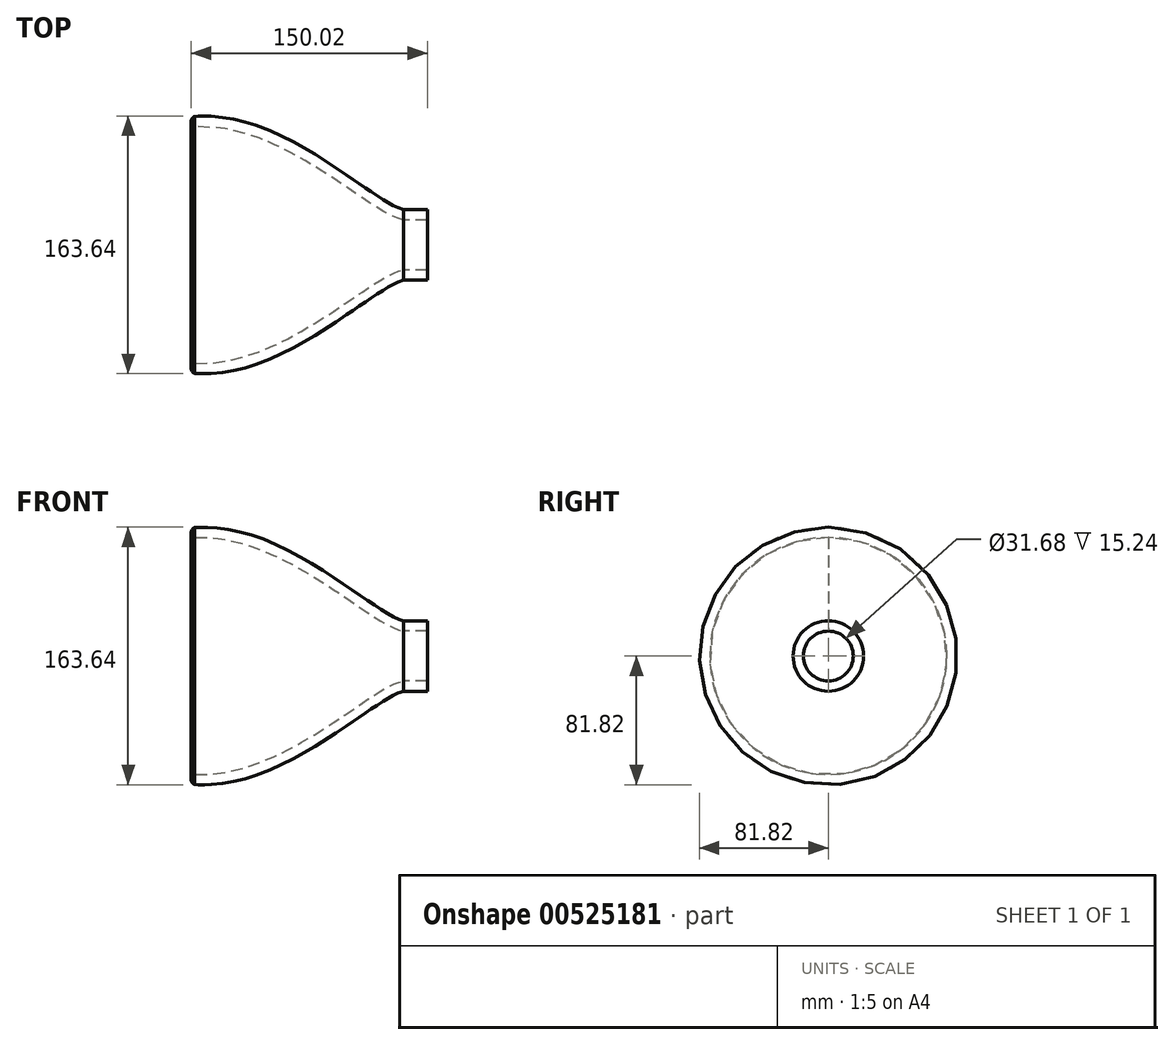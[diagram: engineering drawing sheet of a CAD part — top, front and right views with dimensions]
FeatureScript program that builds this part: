
annotation { "Feature Type Name" : "Feature", "Feature Type Description" : "" }
export const myFeature = defineFeature(function(context is Context, id is Id, definition is map)
    precondition{}
    {
        {
            var Q0;
            Q0=qCreatedBy(makeId("Top.planeOp"),FACE);
            var sketch = newSketch(context, id + "F0", { "sketchPlane" : qUnion([Q0])});
            skLineSegment(sketch, "E0", {"start": v(-136.45, 0) * mm, "end": v(145.54, 0) * mm, "construction": true});
            skLineSegment(sketch, "E1", {"start": v(76.07, 22.38) * mm, "end": v(76.07, 16.02) * mm});
            skLineSegment(sketch, "E2.bottom", {"start": v(76.07, 22.38) * mm, "end": v(91.31, 22.38) * mm});
            skLineSegment(sketch, "E2.top", {"start": v(76.07, 15.84) * mm, "end": v(91.31, 15.84) * mm});
            skLineSegment(sketch, "E2.left", {"start": v(76.07, 22.38) * mm, "end": v(76.07, 15.84) * mm});
            skLineSegment(sketch, "E2.right", {"start": v(91.31, 22.38) * mm, "end": v(91.31, 15.84) * mm});
            skArc(sketch, "E3", {"start": v(-56.47, 81.64) * mm, "mid": v(-58.7, 78.37) * mm, "end": v(-56.2, 75.3) * mm});
            skFitSpline(sketch, "E4", {"points": [v(-56.2, 75.3) * mm, v(76.07, 15.84) * mm], "startDerivative": vector(168.63, 7) * mm, "endDerivative": vector(67.94, -13.53) * mm});
            skFitSpline(sketch, "E5.0", {"points": [v(-56.47, 81.64) * mm, v(-52.68, 81.8) * mm, v(-45.14, 81.6) * mm, v(-30.35, 79.48) * mm, v(-12.51, 74.04) * mm, v(7.6, 64.57) * mm, v(26.2, 53.54) * mm, v(40.2, 44.18) * mm, v(50.34, 37.28) * mm, v(57.35, 32.56) * mm, v(63.71, 28.48) * mm, v(69.33, 25.22) * mm, v(73.26, 23.34) * mm, v(75.82, 22.42) * mm, v(76.86, 22.16) * mm, v(77.31, 22.07) * mm]});
            skSolve(sketch);
        }
        {
            var Q0;
            Q0 = qSketchRegion(id + "F0", true);
            var Q1;
            Q1=sQuery(id+"F0.wireOp",EDGE,"E0");
            revolve(context, id + "F1", {"entities" : qUnion([Q0]), "axis" : qUnion([Q1]), "revolveType" : RevolveType.FULL});
        }
    });
